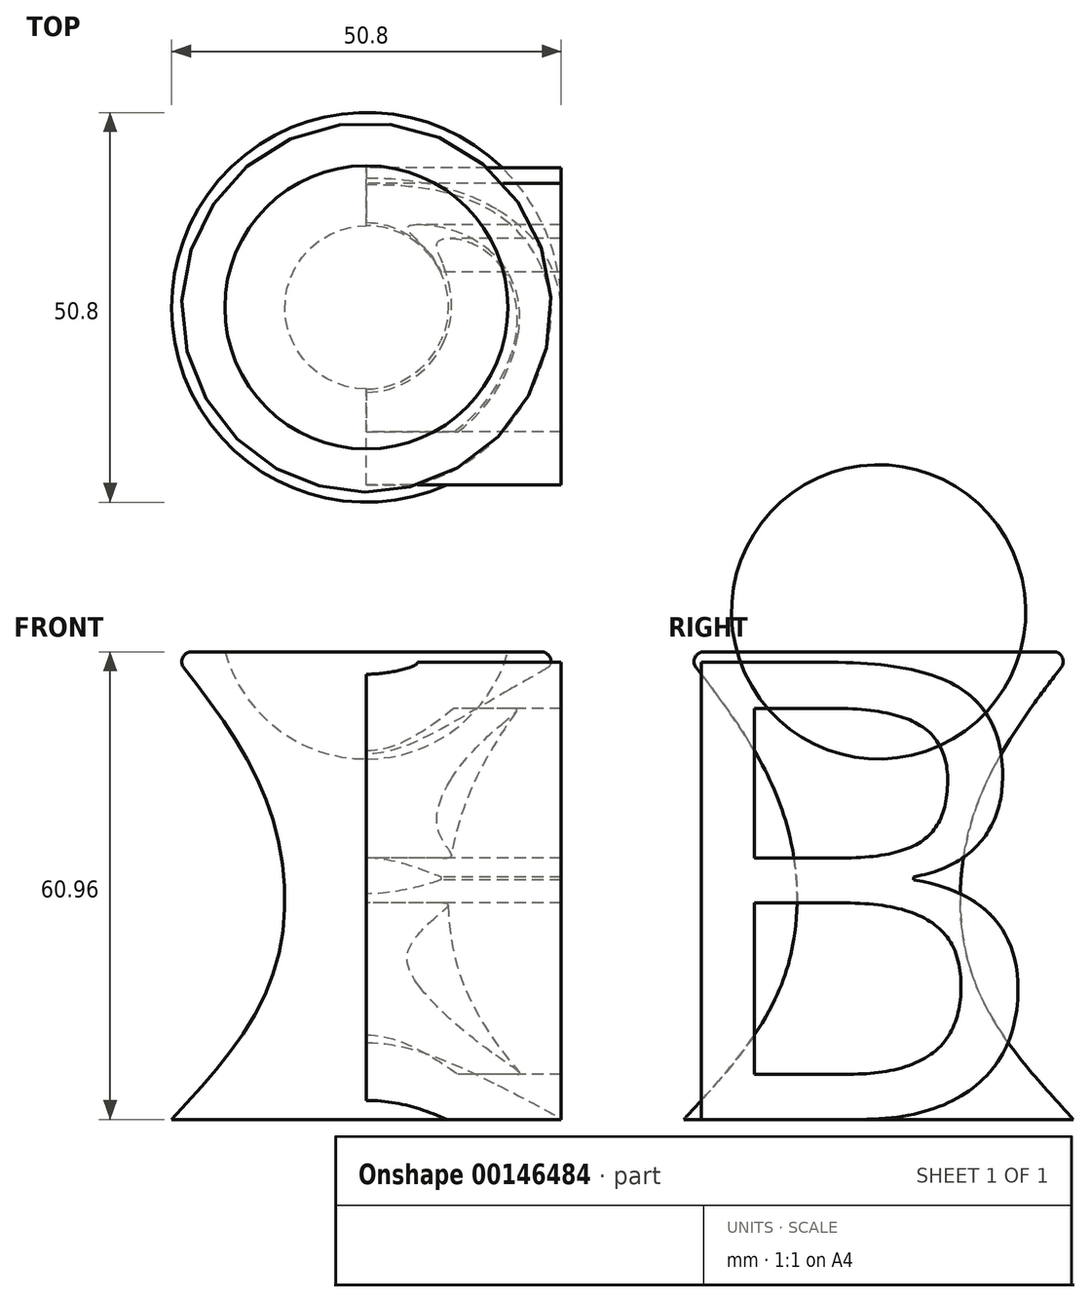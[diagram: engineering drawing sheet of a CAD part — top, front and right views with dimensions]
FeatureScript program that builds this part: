
annotation { "Feature Type Name" : "Feature", "Feature Type Description" : "" }
export const myFeature = defineFeature(function(context is Context, id is Id, definition is map)
    precondition{}
    {
        {
            var Q0;
            Q0=qCreatedBy(makeId("Top.planeOp"),FACE);
            var sketch = newSketch(context, id + "F0", { "sketchPlane" : qUnion([Q0])});
            skCircle(sketch, "E0", {"center": v(0, 0) * mm, "radius": 25.4 * mm});
            skSolve(sketch);
        }
        {
            var Q0;
            Q0 = qSketchRegion(id + "F0", true);
            extrude(context, id + "F1", {"entities" : qUnion([Q0]), "depth" : 60.96 * mm});
        }
        {
            var Q0;
            Q0=qCreatedBy(makeId("Front.planeOp"),FACE);
            var sketch = newSketch(context, id + "F2", { "sketchPlane" : qUnion([Q0])});
            skLineSegment(sketch, "E1", {"start": v(-25.4, 70.05) * mm, "end": v(-25.4, -14.45) * mm});
            skLineSegment(sketch, "E2", {"start": v(-53.42, 60.96) * mm, "end": v(45.9, 60.96) * mm, "construction": true});
            skLineSegment(sketch, "E3", {"start": v(0, 74.91) * mm, "end": v(0, -32.17) * mm, "construction": true});
            skFitSpline(sketch, "E4", {"points": [v(-25.4, 60.96) * mm, v(-12.63, 40.43) * mm, v(-12.38, 18.33) * mm, v(-25.4, 0) * mm], "startDerivative": vector(44.53, -57.09) * mm, "endDerivative": vector(-47.77, -51.82) * mm});
            skLineSegment(sketch, "E5", {"start": v(-25.4, 60.96) * mm, "end": v(-25.4, 0) * mm});
            skSolve(sketch);
        }
        {
            var Q0;
            Q0 = qSketchRegion(id + "F2", true);
            var Q1;
            Q1=sQuery(id+"F2.wireOp",EDGE,"E3");
            revolve(context, id + "F3", {"operationType" : NewBodyOperationType.REMOVE, "entities" : qUnion([Q0]), "axis" : qUnion([Q1]), "revolveType" : RevolveType.FULL, "oppositeDirection" : true});
        }
        {
            var Q0;
            Q0=qCreatedBy(makeId("Right.planeOp"),FACE);
            var sketch = newSketch(context, id + "F4", { "sketchPlane" : qUnion([Q0])});
            skText(sketch, "E6", { "text": "B", "fontName": "OpenSans-Regular.ttf"});
            const initialGuessF4  = {"E6": [-0.03132, 0, 1, 0, 0.0601]};
            skSetInitialGuess(sketch, initialGuessF4);
            skSolve(sketch);
        }
        {
            var Q0;
            Q0 = qSketchRegion(id + "F4", true);
            extrude(context, id + "F5", {"entities" : qUnion([Q0]), "operationType" : NewBodyOperationType.ADD, "depth" : 25.4 * mm});
        }
        {
            var Q0;
            Q0=qCreatedBy(makeId("Right.planeOp"),FACE);
            var sketch = newSketch(context, id + "F6", { "sketchPlane" : qUnion([Q0])});
            skArc(sketch, "E7", {"start": v(0, 46.99) * mm, "mid": v(19.18, 66.17) * mm, "end": v(0, 85.35) * mm});
            skLineSegment(sketch, "E8", {"start": v(0, 85.35) * mm, "end": v(0, 46.99) * mm});
            skSolve(sketch);
        }
        {
            var Q0;
            Q0 = qSketchRegion(id + "F6", true);
            var Q1;
            Q1=sQuery(id+"F6.wireOp",EDGE,"E8");
            revolve(context, id + "F7", {"operationType" : NewBodyOperationType.REMOVE, "entities" : qUnion([Q0]), "axis" : qUnion([Q1]), "revolveType" : RevolveType.FULL, "oppositeDirection" : true});
        }
        {
            var Q0;
            {var subQ0=sQuery(id+"F2.wireOp",EDGE,"E5");var subQ1=sQuery(id+"F2.wireOp",EDGE,"E4");Q0=makeQuery(id+"F3.boolean.opBoolean","MERGE",EDGE,{"derivedFrom":[makeQuery(id+"F1.opExtrude","CAP_EDGE",EDGE,{"disambiguationData":[OSD([sQuery(id+"F0.wireOp",EDGE,"E0")])],"isStart":false}),makeQuery(id+"F3.opRevolve","SWEPT_EDGE",EDGE,{"disambiguationData":[OSD([subQ1,subQ0]),TDD([makeQuery(id+"F2.imprint","INTERSECT",VERTEX,{"disambiguationData":[OD(0.0)],"derivedFrom":[subQ1,subQ0]})])]})]});}
            fillet(context, id + "F8", {"entities" : qUnion([Q0]), "radius" : 1.27 * mm, "tangentPropagation" : true, "allowEdgeOverflow" : false});
        }
    });
